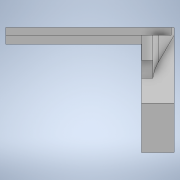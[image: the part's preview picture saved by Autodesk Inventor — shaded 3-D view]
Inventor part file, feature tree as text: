
AUTODESK INVENTOR PART (.ipt)
format: ipt  version: 2022 (Build 260153000, 153)  size: 231,936 bytes
history: native  units: in
note: dims shown in document units (in); Inventor stores cm internally (conversion verified against a paired STEP export)
features: extrude x7, sketch x7, fillet x3
ambient origin geometry x8: Origin, YZ Plane, XZ Plane, XY Plane, X Axis, Y Axis, Z Axis, Center Point
bodies: Solid1 (feature_tree)
feature tree (17):
  extrude  "Extrusion1"  Depth=0.122in
  extrude  "Extrusion2"  Depth=0.1181in
  extrude  "Extrusion3"  Depth=0.2362in TaperAngle=0.0deg
  extrude  "Extrusion4"  Depth=0.0787in
  extrude  "Extrusion5"  Depth=0.315in
  extrude  "Extrusion6"  Depth=0.3937in
  extrude  "Extrusion7"  Depth=0.1181in
  fillet  "Fillet1"  [1 undecoded]
  fillet  "Fillet2"  Radius=0.9843in
  fillet  "Fillet3"  Radius=0.4331in
  sketch  "Sketch1"  dims[d1=0.6693in d2=0.122in]
  sketch  "Sketch2"  dims[d3=0.1181in d4=0.1181in]
  sketch  "Sketch3"  dims[d5=0.2441in d6=0.2362in d7=0.0in]
  sketch  "Sketch4"  dims[d8=0.122in d9=0.0787in]
  sketch  "Sketch6"  dims[d10=0.2362in d11=0.0in d13=0.315in]
  sketch  "Sketch7"  dims[d14=0.3937in d15=0.0in d17=0.5118in]
  sketch  "Sketch8"  dims[d18=0.4921in d19=0.0362in d20=0.0in d21=0.9843in d22=0.4331in d23=0.2165in d24=0.2165in d25=0.1969in d26=0.3937in d27=0.2953in d28=0.1181in d29=0.0787in d30=0.0787in d31=0.0669in d32=0.0in d33=0.4724in d34=0.2756in d35=0.1575in d36=0.0787in d37=0.0787in d38=0.0in d39=0.3543in d40=0.0in d41=0.3543in d42=0.1543in d43=0.4209in d44=0.0in d45=0.0in d46=0.0551in d47=0.0in d48=0.0787in d49=0.2362in d50=0.0787in d51=0.748in d52=0.1181in]
note: 1 required parameter value undecoded (feature->parameter linkage not recoverable at this tier; creation-order binding heuristic only, values carry confidence <= 0.55)
